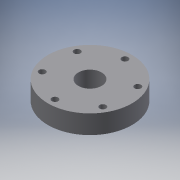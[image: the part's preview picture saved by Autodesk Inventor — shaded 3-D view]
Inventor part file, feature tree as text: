
AUTODESK INVENTOR PART (.ipt)
format: ipt  version: 2016 (Build 200138000, 138)  size: 115,712 bytes
history: native  units: in
note: dims shown in document units (in); Inventor stores cm internally (conversion verified against a paired STEP export)
features: extrude x1, sketch x1
ambient origin geometry x8: Origin, YZ Plane, XZ Plane, XY Plane, X Axis, Y Axis, Z Axis, Center Point
bodies: Body1 (feature_tree)
feature tree (2):
  extrude  "Extrusion2"  Depth=0.503in
  sketch  "Sketch1"  dims[d0=1.875in d1=0.17in d2=0.17in d3=0.17in d4=0.17in d5=0.17in d6=0.17in d7=2.25in d10=0.625in d11=0.503in d12=0.0in]
